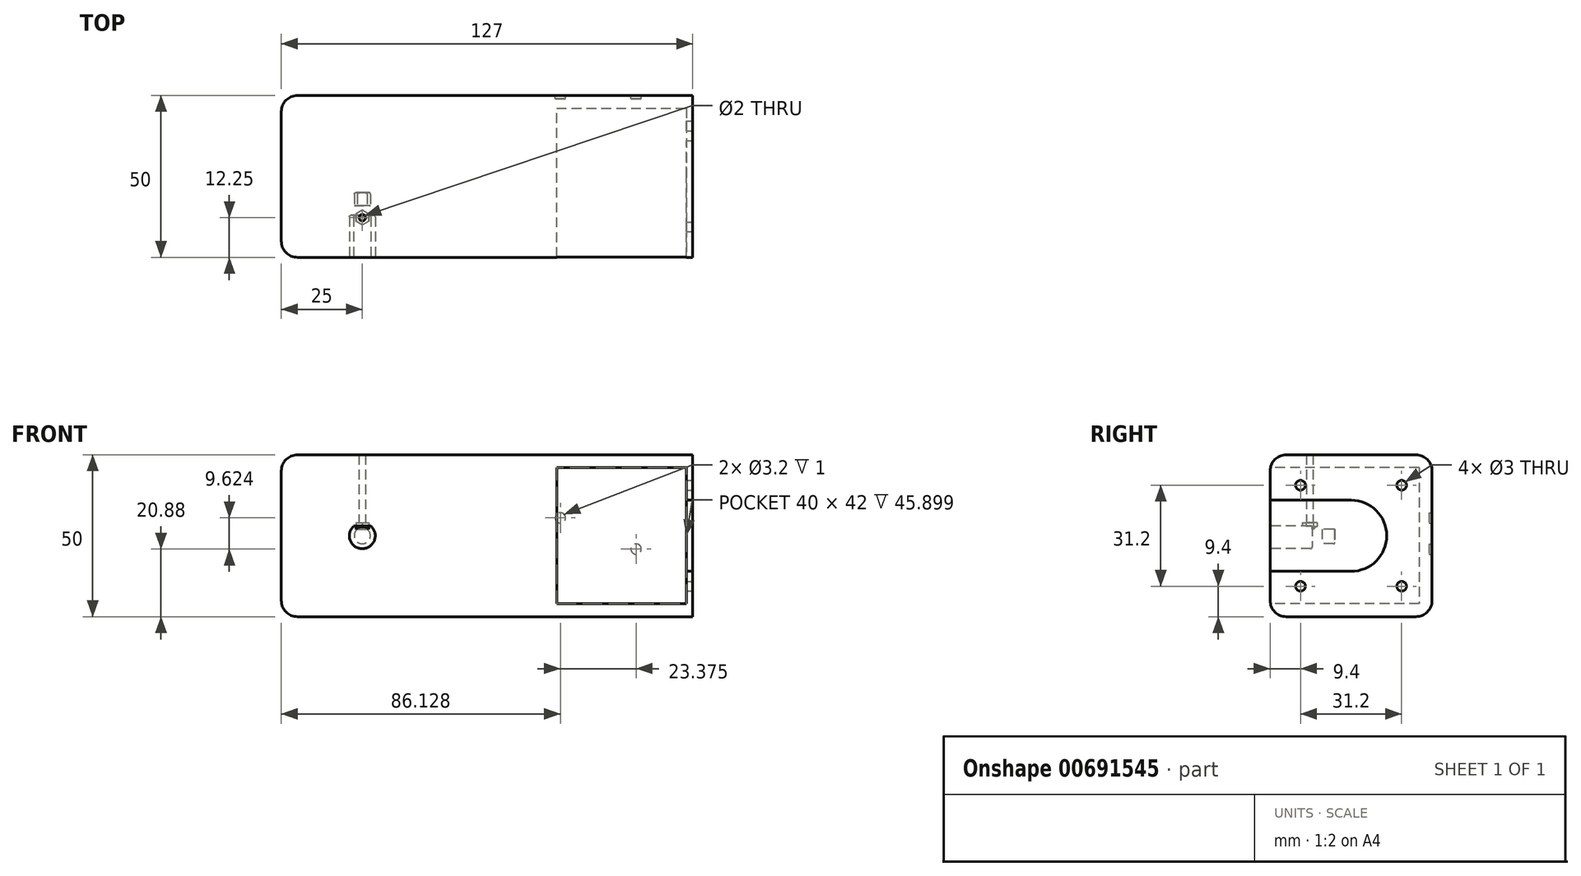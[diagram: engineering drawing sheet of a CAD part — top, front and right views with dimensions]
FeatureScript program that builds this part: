
annotation { "Feature Type Name" : "Feature", "Feature Type Description" : "" }
export const myFeature = defineFeature(function(context is Context, id is Id, definition is map)
    precondition{}
    {
        {
            var Q0;
            Q0=qCreatedBy(makeId("Front.planeOp"),FACE);
            var sketch = newSketch(context, id + "F0", { "sketchPlane" : qUnion([Q0])});
            skLineSegment(sketch, "E0.bottom", {"start": v(63.5, -25) * mm, "end": v(-63.5, -25) * mm});
            skLineSegment(sketch, "E0.top", {"start": v(63.5, 25) * mm, "end": v(-63.5, 25) * mm});
            skLineSegment(sketch, "E0.left", {"start": v(63.5, -25) * mm, "end": v(63.5, 25) * mm});
            skLineSegment(sketch, "E0.right", {"start": v(-63.5, -25) * mm, "end": v(-63.5, 25) * mm});
            skPoint(sketch, "E0.middle", {"position": v(0, 0) * mm});
            skSolve(sketch);
        }
        {
            var Q0;
            Q0=qSketchRegion(id+"F0",true);
            extrude(context, id + "F1", {"entities" : qUnion([Q0]), "depth" : 50 * mm, "offsetDistance" : 25 * mm});
        }
        {
            var Q0;
            Q0=makeQuery(id+"F1.opExtrude","SWEPT_FACE",FACE,{"disambiguationData":[OSD([sQuery(id+"F0.wireOp",EDGE,"E0.left")])]});
            var sketch = newSketch(context, id + "F2", { "sketchPlane" : qUnion([Q0])});
            skLineSegment(sketch, "E1", {"start": v(-46, 16.76) * mm, "end": v(-41.76, 21) * mm});
            skLineSegment(sketch, "E2", {"start": v(-41.76, 21) * mm, "end": v(-8.24, 21) * mm});
            skLineSegment(sketch, "E3", {"start": v(-8.24, 21) * mm, "end": v(-4, 16.76) * mm});
            skLineSegment(sketch, "E4", {"start": v(-4, 16.76) * mm, "end": v(-4, -16.76) * mm});
            skLineSegment(sketch, "E5", {"start": v(-4, -16.76) * mm, "end": v(-8.24, -21) * mm});
            skLineSegment(sketch, "E6", {"start": v(-8.24, -21) * mm, "end": v(-41.76, -21) * mm});
            skLineSegment(sketch, "E7", {"start": v(-41.76, -21) * mm, "end": v(-46, -16.76) * mm});
            skLineSegment(sketch, "E8", {"start": v(-46, -16.76) * mm, "end": v(-46, 16.76) * mm});
            skLineSegment(sketch, "E9", {"start": v(-25, 21) * mm, "end": v(-25, 25) * mm, "construction": true});
            skLineSegment(sketch, "E10", {"start": v(-25, -21) * mm, "end": v(-25, -25) * mm, "construction": true});
            skLineSegment(sketch, "E11", {"start": v(-46, 0) * mm, "end": v(-50, 0) * mm, "construction": true});
            skLineSegment(sketch, "E12", {"start": v(0, 0) * mm, "end": v(-4, 0) * mm, "construction": true});
            skSolve(sketch);
        }
        {
            var Q0;
            Q0=qSketchRegion(id+"F2",true);
            extrude(context, id + "F3", {"entities" : qUnion([Q0]), "operationType" : NewBodyOperationType.REMOVE, "oppositeDirection" : true, "depth" : 42 * mm, "offsetDistance" : 25 * mm});
        }
        {
            var Q0;
            Q0=makeQuery(id+"F1.opExtrude","CAP_FACE",FACE,{"disambiguationData":[OSD([sQuery(id+"F0.wireOp",EDGE,"E0.bottom"),sQuery(id+"F0.wireOp",EDGE,"E0.top"),sQuery(id+"F0.wireOp",EDGE,"E0.left"),sQuery(id+"F0.wireOp",EDGE,"E0.right")])],"isStart":false});
            var sketch = newSketch(context, id + "F4", { "sketchPlane" : qUnion([Q0])});
            skCircle(sketch, "E13", {"center": v(-38.5, 0) * mm, "radius": 11 * mm});
            skSolve(sketch);
        }
        {
            var Q0;
            Q0=qSketchRegion(id+"F4",true);
            extrude(context, id + "F5", {"entities" : qUnion([Q0]), "operationType" : NewBodyOperationType.REMOVE, "oppositeDirection" : true, "depth" : 5 * mm, "offsetDistance" : 25 * mm});
        }
        {
            var Q0;
            Q0=makeQuery(id+"F5.boolean.opBoolean","COPY",FACE,{"derivedFrom":makeQuery(id+"F5.opExtrude","CAP_FACE",FACE,{"disambiguationData":[OSD([sQuery(id+"F4.wireOp",EDGE,"E13")])],"isStart":false})});
            var sketch = newSketch(context, id + "F6", { "sketchPlane" : qUnion([Q0])});
            skArc(sketch, "E14", {"start": v(-40, 2) * mm, "mid": v(-38.5, -2.5) * mm, "end": v(-37, 2) * mm});
            skLineSegment(sketch, "E15", {"start": v(-40, 2) * mm, "end": v(-37, 2) * mm});
            skSolve(sketch);
        }
        {
            var Q0;
            Q0=qSketchRegion(id+"F6",true);
            extrude(context, id + "F7", {"entities" : qUnion([Q0]), "operationType" : NewBodyOperationType.REMOVE, "oppositeDirection" : true, "depth" : 15 * mm, "offsetDistance" : 25 * mm});
        }
        {
            var Q0;
            Q0=makeQuery(id+"F7.boolean.opBoolean","COPY",EDGE,{"derivedFrom":makeQuery(id+"F7.opExtrude","CAP_EDGE",EDGE,{"disambiguationData":[OSD([sQuery(id+"F6.wireOp",EDGE,"E14")])],"isStart":false})});
            fillet(context, id + "F8", {"entities" : qUnion([Q0]), "radius" : .5 * mm, "tangentPropagation" : true, "allowEdgeOverflow" : false});
        }
        {
            var Q0;
            Q0=makeQuery(id+"F1.opExtrude","CAP_EDGE",EDGE,{"disambiguationData":[OSD([sQuery(id+"F0.wireOp",EDGE,"E0.top")])],"isStart":false});
            var Q1;
            Q1=makeQuery(id+"F1.opExtrude","CAP_EDGE",EDGE,{"disambiguationData":[OSD([sQuery(id+"F0.wireOp",EDGE,"E0.bottom")])],"isStart":false});
            var Q2;
            Q2=makeQuery(id+"F1.opExtrude","CAP_EDGE",EDGE,{"disambiguationData":[OSD([sQuery(id+"F0.wireOp",EDGE,"E0.top")])],"isStart":true});
            var Q3;
            Q3=makeQuery(id+"F1.opExtrude","CAP_EDGE",EDGE,{"disambiguationData":[OSD([sQuery(id+"F0.wireOp",EDGE,"E0.bottom")])],"isStart":true});
            var Q4;
            Q4=makeQuery(id+"F1.opExtrude","SWEPT_EDGE",EDGE,{"disambiguationData":[OSD([sQuery(id+"F0.wireOp",EDGE,"E0.top"),sQuery(id+"F0.wireOp",EDGE,"E0.right")])]});
            var Q5;
            Q5=makeQuery(id+"F1.opExtrude","SWEPT_EDGE",EDGE,{"disambiguationData":[OSD([sQuery(id+"F0.wireOp",EDGE,"E0.bottom"),sQuery(id+"F0.wireOp",EDGE,"E0.right")])]});
            var Q6;
            Q6=makeQuery(id+"F1.opExtrude","CAP_EDGE",EDGE,{"disambiguationData":[OSD([sQuery(id+"F0.wireOp",EDGE,"E0.right")])],"isStart":true});
            var Q7;
            Q7=makeQuery(id+"F1.opExtrude","CAP_EDGE",EDGE,{"disambiguationData":[OSD([sQuery(id+"F0.wireOp",EDGE,"E0.right")])],"isStart":false});
            fillet(context, id + "F9", {"entities" : qUnion([Q0, Q1, Q2, Q3, Q4, Q5, Q6, Q7]), "radius" : 5 * mm, "tangentPropagation" : true, "allowEdgeOverflow" : false});
        }
        {
            var Q0;
            Q0=makeQuery(id+"F1.opExtrude","SWEPT_FACE",FACE,{"disambiguationData":[OSD([sQuery(id+"F0.wireOp",EDGE,"E0.left")])]});
            var sketch = newSketch(context, id + "F10", { "sketchPlane" : qUnion([Q0])});
            skPoint(sketch, "E16.middle", {"position": v(-25, 0) * mm});
            skLineSegment(sketch, "E17", {"start": v(-46, -16.76) * mm, "end": v(-41.76, -21) * mm});
            skLineSegment(sketch, "E18", {"start": v(-46, -16.76) * mm, "end": v(-46, 16.76) * mm});
            skLineSegment(sketch, "E19", {"start": v(-46, 16.76) * mm, "end": v(-41.76, 21) * mm});
            skLineSegment(sketch, "E20", {"start": v(-41.76, -21) * mm, "end": v(-8.24, -21) * mm});
            skLineSegment(sketch, "E21", {"start": v(-8.24, -21) * mm, "end": v(-4, -16.76) * mm});
            skLineSegment(sketch, "E22", {"start": v(-4, -16.76) * mm, "end": v(-4, 16.76) * mm});
            skLineSegment(sketch, "E23", {"start": v(-4, 16.76) * mm, "end": v(-8.24, 21) * mm});
            skLineSegment(sketch, "E24", {"start": v(-8.24, 21) * mm, "end": v(-41.76, 21) * mm});
            skLineSegment(sketch, "E25", {"start": v(-25, 0) * mm, "end": v(-4, 0) * mm, "construction": true});
            skLineSegment(sketch, "E26", {"start": v(-25, 0) * mm, "end": v(-25, 21) * mm, "construction": true});
            skLineSegment(sketch, "E27", {"start": v(-25, 0) * mm, "end": v(-25, -21) * mm, "construction": true});
            skLineSegment(sketch, "E28", {"start": v(-25, 0) * mm, "end": v(-46, 0) * mm, "construction": true});
            skLineSegment(sketch, "E29.bottom", {"start": v(-9.4, -15.6) * mm, "end": v(-40.6, -15.6) * mm});
            skLineSegment(sketch, "E29.top", {"start": v(-9.4, 15.6) * mm, "end": v(-40.6, 15.6) * mm});
            skLineSegment(sketch, "E29.left", {"start": v(-9.4, -15.6) * mm, "end": v(-9.4, 15.6) * mm});
            skLineSegment(sketch, "E29.right", {"start": v(-40.6, -15.6) * mm, "end": v(-40.6, 15.6) * mm});
            skCircle(sketch, "E30", {"center": v(-40.6, 15.6) * mm, "radius": 1.5 * mm});
            skCircle(sketch, "E31", {"center": v(-9.4, 15.6) * mm, "radius": 1.5 * mm});
            skCircle(sketch, "E32", {"center": v(-9.4, -15.6) * mm, "radius": 1.5 * mm});
            skCircle(sketch, "E33", {"center": v(-40.6, -15.6) * mm, "radius": 1.5 * mm});
            skLineSegment(sketch, "E34.bottom", {"start": v(-33.1, 21) * mm, "end": v(-16.9, 21) * mm});
            skLineSegment(sketch, "E35", {"start": v(-16.9, 21) * mm, "end": v(-8.24, 21) * mm, "construction": true});
            skLineSegment(sketch, "E36", {"start": v(-33.1, 21) * mm, "end": v(-41.76, 21) * mm, "construction": true});
            skSolve(sketch);
        }
        {
            var Q0;
            Q0=makeQuery(id+"FMPlXjMWnGon0a9_1.boolean.opBoolean","MERGE",FACE,{"derivedFrom":[makeQuery(id+"F1.opExtrude","SWEPT_FACE",FACE,{"disambiguationData":[OSD([sQuery(id+"F0.wireOp",EDGE,"E0.left")])]}),makeQuery(id+"FMPlXjMWnGon0a9_1.opExtrude","CAP_FACE",FACE,{"disambiguationData":[OSD([sQuery(id+"F10.wireOp",EDGE,"7e317716-1d10-45a1-bd77-1f030e6113fa"),sQuery(id+"F10.wireOp",EDGE,"a9baf04a-07a7-4197-b8e6-3b8d32bb72bb"),sQuery(id+"F10.wireOp",EDGE,"0afc13e5-a02a-4f5f-93d0-e888419d06cc"),sQuery(id+"F10.wireOp",EDGE,"3bec6db8-7ce1-4d02-bc73-26e9fa90f9ca"),sQuery(id+"F10.wireOp",EDGE,"4aacd247-3ff8-4e3c-a909-91dfdb2c83a4"),sQuery(id+"F10.wireOp",EDGE,"cb9adce3-904a-4ef7-b8bb-e01b4716a234"),sQuery(id+"F10.wireOp",EDGE,"422983aa-e8dd-4766-8909-e12d55b331f8"),sQuery(id+"F10.wireOp",EDGE,"0b41c461-bc85-4d50-8d82-77dba81586c2"),sQuery(id+"F10.wireOp",EDGE,"d2e1f196-5fb4-45e0-a0eb-1cf5d613c0ba"),sQuery(id+"F10.wireOp",EDGE,"4a6b8d65-2de6-42a6-bc2a-ce8d35ed1551"),sQuery(id+"F10.wireOp",EDGE,"09a8e3e9-80f5-4af3-9dc7-d9ba060c69f5"),sQuery(id+"F10.wireOp",EDGE,"eed8e5a7-c47a-4f85-b74d-ca0ec0753e29"),sQuery(id+"F10.wireOp",EDGE,"10ccaaaf-dc0f-476e-ab06-8ddfde2fb4c6")])],"isStart":true})]});
            var sketch = newSketch(context, id + "F11", { "sketchPlane" : qUnion([Q0])});
            skLineSegment(sketch, "E37", {"start": v(-25, -11) * mm, "end": v(-50, -11) * mm});
            skLineSegment(sketch, "E38", {"start": v(-25, 11) * mm, "end": v(-50, 11) * mm});
            skArc(sketch, "E39", {"start": v(-25, -11) * mm, "mid": v(-14, 0) * mm, "end": v(-25, 11) * mm});
            skLineSegment(sketch, "E40", {"start": v(-50, 11) * mm, "end": v(-50, -11) * mm});
            skSolve(sketch);
        }
        {
            var Q0;
            Q0=makeQuery(id+"F1.opExtrude","CAP_FACE",FACE,{"disambiguationData":[OSD([sQuery(id+"F0.wireOp",EDGE,"E0.bottom"),sQuery(id+"F0.wireOp",EDGE,"E0.top"),sQuery(id+"F0.wireOp",EDGE,"E0.left"),sQuery(id+"F0.wireOp",EDGE,"E0.right")])],"isStart":false});
            var sketch = newSketch(context, id + "F12", { "sketchPlane" : qUnion([Q0])});
            skLineSegment(sketch, "E41.bottom", {"start": v(21.5, 21) * mm, "end": v(61.5, 21) * mm});
            skLineSegment(sketch, "E41.top", {"start": v(21.5, -21) * mm, "end": v(61.5, -21) * mm});
            skLineSegment(sketch, "E41.left", {"start": v(21.5, 21) * mm, "end": v(21.5, -21) * mm});
            skLineSegment(sketch, "E41.right", {"start": v(61.5, 21) * mm, "end": v(61.5, -21) * mm});
            skLineSegment(sketch, "E42", {"start": v(61.5, 21) * mm, "end": v(61.5, 25) * mm, "construction": true});
            skLineSegment(sketch, "E43", {"start": v(63.5, -21) * mm, "end": v(63.5, -25) * mm, "construction": true});
            skSolve(sketch);
        }
        {
            var Q0;
            Q0=qSketchRegion(id+"F12",true);
            extrude(context, id + "F13", {"entities" : qUnion([Q0]), "operationType" : NewBodyOperationType.REMOVE, "oppositeDirection" : true, "depth" : 46 * mm, "offsetDistance" : 25 * mm});
        }
        {
            var Q0;
            Q0=makeQuery(id+"F1.opExtrude","CAP_FACE",FACE,{"disambiguationData":[OSD([sQuery(id+"F0.wireOp",EDGE,"E0.bottom"),sQuery(id+"F0.wireOp",EDGE,"E0.top"),sQuery(id+"F0.wireOp",EDGE,"E0.left"),sQuery(id+"F0.wireOp",EDGE,"E0.right")])],"isStart":true});
            var sketch = newSketch(context, id + "F14", { "sketchPlane" : qUnion([Q0])});
            skCircle(sketch, "E44", {"center": v(-22.63, 5.5) * mm, "radius": 1.6 * mm});
            skCircle(sketch, "E45", {"center": v(-46, -4.12) * mm, "radius": 1.6 * mm});
            skLineSegment(sketch, "E46.left", {"start": v(-22.5, 8) * mm, "end": v(-45.33, 9.15) * mm});
            skLineSegment(sketch, "E46.right", {"start": v(-23.3, -7.77) * mm, "end": v(-46.13, -6.62) * mm});
            skLineSegment(sketch, "E47", {"start": v(-20.13, 5.38) * mm, "end": v(-20.68, -5.4) * mm});
            skLineSegment(sketch, "E48", {"start": v(-47.96, 6.78) * mm, "end": v(-48.5, -4) * mm});
            skArc(sketch, "E49", {"start": v(-20.13, 5.38) * mm, "mid": v(-20.77, 7.18) * mm, "end": v(-22.5, 8) * mm});
            skArc(sketch, "E50", {"start": v(-23.3, -7.77) * mm, "mid": v(-21.5, -7.13) * mm, "end": v(-20.68, -5.4) * mm});
            skArc(sketch, "E51", {"start": v(-45.33, 9.15) * mm, "mid": v(-47.14, 8.51) * mm, "end": v(-47.96, 6.78) * mm});
            skArc(sketch, "E52", {"start": v(-48.5, -4) * mm, "mid": v(-47.86, -5.8) * mm, "end": v(-46.13, -6.62) * mm});
            skSolve(sketch);
        }
        {
            var Q0;
            Q0=makeQuery(id+"F14.imprint","IMPRINT",FACE,{"disambiguationData":[TD([[makeQuery(id+"F14.imprint","IMPRINT",EDGE,{"derivedFrom":sQuery(id+"F14.wireOp",EDGE,"E45")}),1.0]])]});
            var Q1;
            Q1=makeQuery(id+"F14.imprint","IMPRINT",FACE,{"disambiguationData":[TD([[makeQuery(id+"F14.imprint","IMPRINT",EDGE,{"derivedFrom":sQuery(id+"F14.wireOp",EDGE,"E44")}),1.0]])]});
            extrude(context, id + "F15", {"entities" : qUnion([Q0, Q1]), "operationType" : NewBodyOperationType.REMOVE, "oppositeDirection" : true, "depth" : 1 * mm, "offsetDistance" : 25 * mm});
        }
        {
            var Q0;
            Q0=makeQuery(id+"F7.boolean.opBoolean","COPY",FACE,{"derivedFrom":makeQuery(id+"F7.opExtrude","SWEPT_FACE",FACE,{"disambiguationData":[OSD([sQuery(id+"F6.wireOp",EDGE,"E15")])]})});
            var sketch = newSketch(context, id + "F16", { "sketchPlane" : qUnion([Q0])});
            skCircle(sketch, "E53", {"center": v(-38.5, 37.75) * mm, "radius": 1 * mm});
            skLineSegment(sketch, "E54", {"start": v(-38.5, 45) * mm, "end": v(-38.5, 30.5) * mm, "construction": true});
            skCircle(sketch, "E55.cCircle", {"center": v(-38.5, 37.75) * mm, "radius": 2 * mm, "construction": true});
            skLineSegment(sketch, "E55.0", {"start": v(-38.5, 40.06) * mm, "end": v(-36.5, 38.9) * mm});
            skLineSegment(sketch, "E55.1", {"start": v(-36.5, 38.9) * mm, "end": v(-36.5, 36.6) * mm});
            skLineSegment(sketch, "E55.2", {"start": v(-36.5, 36.6) * mm, "end": v(-38.5, 35.44) * mm});
            skLineSegment(sketch, "E55.3", {"start": v(-38.5, 35.44) * mm, "end": v(-40.5, 36.6) * mm});
            skLineSegment(sketch, "E55.4", {"start": v(-40.5, 36.6) * mm, "end": v(-40.5, 38.9) * mm});
            skLineSegment(sketch, "E55.5", {"start": v(-40.5, 38.9) * mm, "end": v(-38.5, 40.06) * mm});
            skPoint(sketch, "E55.0.midPoint", {"position": v(-37.5, 39.48) * mm});
            skSolve(sketch);
        }
        {
            var Q0;
            Q0=qSketchRegion(id+"F16",true);
            extrude(context, id + "F17", {"entities" : qUnion([Q0]), "operationType" : NewBodyOperationType.REMOVE, "oppositeDirection" : true, "depth" : 2 * mm, "offsetDistance" : 25 * mm, "hasSecondDirection" : true, "secondDirectionOppositeDirection" : false, "secondDirectionDepth" : 1.03 * mm});
        }
        {
            var Q0;
            Q0=makeQuery(id+"F17.boolean.opBoolean","SPLIT",FACE,{"disambiguationData":[TD([makeQuery(id+"F17.opExtrude","SWEPT_FACE",FACE,{"disambiguationData":[OSD([sQuery(id+"F16.wireOp",EDGE,"E53")])]})])],"derivedFrom":makeQuery(id+"F7.boolean.opBoolean","COPY",FACE,{"derivedFrom":makeQuery(id+"F7.opExtrude","SWEPT_FACE",FACE,{"disambiguationData":[OSD([sQuery(id+"F6.wireOp",EDGE,"E15")])]})})});
            extrude(context, id + "F18", {"entities" : qUnion([Q0]), "operationType" : NewBodyOperationType.REMOVE, "oppositeDirection" : true, "depth" : 25 * mm, "offsetDistance" : 25 * mm});
        }
        {
            var Q0;
            Q0=makeQuery(id+"F10.imprint","IMPRINT",FACE,{"disambiguationData":[TD([[makeQuery(id+"F10.imprint","IMPRINT",EDGE,{"derivedFrom":sQuery(id+"F10.wireOp",EDGE,"E17")}),-1.0]])]});
            var Q1;
            {var subQ5=sQuery(id+"F10.wireOp",EDGE,"E32");var subQ10=sQuery(id+"F10.wireOp",EDGE,"E29.bottom");var subQ15=makeQuery(id+"F10.imprint","INTERSECT",VERTEX,{"derivedFrom":[subQ10,subQ5]});Q1=makeQuery(id+"F10.imprint","IMPRINT",FACE,{"disambiguationData":[TD([[makeQuery(id+"F10.imprint","IMPRINT",EDGE,{"disambiguationData":[TD([[subQ15,-1.0]])],"derivedFrom":subQ10}),-1.0]])]});}
            extrude(context, id + "F19", {"entities" : qUnion([Q0, Q1]), "operationType" : NewBodyOperationType.ADD, "oppositeDirection" : true, "depth" : 2 * mm, "offsetDistance" : 25 * mm});
        }
        {
            var Q0;
            {var subQ0=sQuery(id+"F11.wireOp",EDGE,"E39");Q0=makeQuery(id+"F11.imprint","IMPRINT",FACE,{"disambiguationData":[TD([[makeQuery(id+"F11.imprint","IMPRINT",EDGE,{"derivedFrom":subQ0}),1.0]])]});}
            var Q1;
            {var subQ0=sQuery(id+"F11.wireOp",EDGE,"E40");Q1=makeQuery(id+"F11.imprint","IMPRINT",FACE,{"disambiguationData":[TD([[makeQuery(id+"F11.imprint","IMPRINT",EDGE,{"derivedFrom":subQ0}),-1.0]])]});}
            extrude(context, id + "F20", {"entities" : qUnion([Q0, Q1]), "operationType" : NewBodyOperationType.REMOVE, "oppositeDirection" : true, "depth" : 25 * mm, "offsetDistance" : 25 * mm});
        }
        {
            var Q0;
            Q0=makeQuery(id+"F5.boolean.opBoolean","COPY",FACE,{"derivedFrom":makeQuery(id+"F5.opExtrude","CAP_FACE",FACE,{"disambiguationData":[OSD([sQuery(id+"F4.wireOp",EDGE,"E13")])],"isStart":false})});
            var sketch = newSketch(context, id + "F21", { "sketchPlane" : qUnion([Q0])});
            skArc(sketch, "E56", {"start": v(-41.15, 3) * mm, "mid": v(-38.5, -4) * mm, "end": v(-35.85, 3) * mm});
            skLineSegment(sketch, "E57", {"start": v(-41.15, 3) * mm, "end": v(-35.85, 3) * mm});
            skSolve(sketch);
        }
        {
            var Q0;
            Q0 = qSketchRegion(id + "F21", true);
            extrude(context, id + "F22", {"entities" : qUnion([Q0]), "operationType" : NewBodyOperationType.REMOVE, "oppositeDirection" : true, "depth" : 8 * mm, "offsetDistance" : 25 * mm});
        }
        {
            var Q0;
            Q0=makeQuery(id+"F22.boolean.opBoolean","COPY",FACE,{"derivedFrom":makeQuery(id+"F22.opExtrude","CAP_FACE",FACE,{"disambiguationData":[OSD([sQuery(id+"F21.wireOp",EDGE,"E56"),sQuery(id+"F21.wireOp",EDGE,"E57")])],"isStart":false})});
            var sketch = newSketch(context, id + "F23", { "sketchPlane" : qUnion([Q0])});
            skCircle(sketch, "E58", {"center": v(-38.5, 0) * mm, "radius": 2.81 * mm});
            skSolve(sketch);
        }
        {
            var Q0;
            Q0 = qSketchRegion(id + "F23", true);
            extrude(context, id + "F24", {"entities" : qUnion([Q0]), "operationType" : NewBodyOperationType.ADD, "oppositeDirection" : true, "depth" : 3 * mm, "offsetDistance" : 25 * mm});
        }
        {
            var Q0;
            Q0=makeQuery(id+"F22.boolean.opBoolean","COPY",EDGE,{"derivedFrom":makeQuery(id+"F22.opExtrude","CAP_EDGE",EDGE,{"disambiguationData":[OSD([sQuery(id+"F21.wireOp",EDGE,"E56")])],"isStart":false})});
            fillet(context, id + "F25", {"entities" : qUnion([Q0]), "radius" : .5 * mm, "tangentPropagation" : true, "allowEdgeOverflow" : false});
        }
        {
            var Q0;
            Q0=makeQuery(id+"F5.boolean.opBoolean","COPY",FACE,{"derivedFrom":makeQuery(id+"F5.opExtrude","CAP_FACE",FACE,{"disambiguationData":[OSD([sQuery(id+"F4.wireOp",EDGE,"E13")])],"isStart":false})});
            var sketch = newSketch(context, id + "F26", { "sketchPlane" : qUnion([Q0])});
            skArc(sketch, "E59", {"start": v(-41.15, 3) * mm, "mid": v(-38.5, -4) * mm, "end": v(-35.85, 3) * mm});
            skLineSegment(sketch, "E60", {"start": v(-35.85, 3) * mm, "end": v(-41.15, 3) * mm});
            skCircle(sketch, "E61", {"center": v(-38.5, 0) * mm, "radius": 11 * mm});
            skSolve(sketch);
        }
        {
            var Q0;
            Q0 = qSketchRegion(id + "F26", true);
            var Q1;
            {var subQ0=sQuery(id+"F0.wireOp",EDGE,"E0.right");var subQ1=sQuery(id+"F0.wireOp",EDGE,"E0.top");var subQ2=sQuery(id+"F0.wireOp",EDGE,"E0.bottom");Q1=makeQuery(id+"F13.boolean.opBoolean","SPLIT",FACE,{"disambiguationData":[TD([makeQuery(id+"F5.boolean.opBoolean","COPY",FACE,{"derivedFrom":makeQuery(id+"F5.opExtrude","SWEPT_FACE",FACE,{"disambiguationData":[OSD([sQuery(id+"F4.wireOp",EDGE,"E13")])]})})])],"derivedFrom":makeQuery(id+"F1.opExtrude","CAP_FACE",FACE,{"disambiguationData":[OSD([subQ2,subQ1,sQuery(id+"F0.wireOp",EDGE,"E0.left"),subQ0])],"isStart":false})});}
            extrude(context, id + "F27", {"entities" : qUnion([Q0]), "operationType" : NewBodyOperationType.ADD, "endBound" : BoundingType.UP_TO_SURFACE, "depth" : 25 * mm, "endBoundEntityFace" : qUnion([Q1]), "offsetDistance" : 25 * mm});
        }
    });
